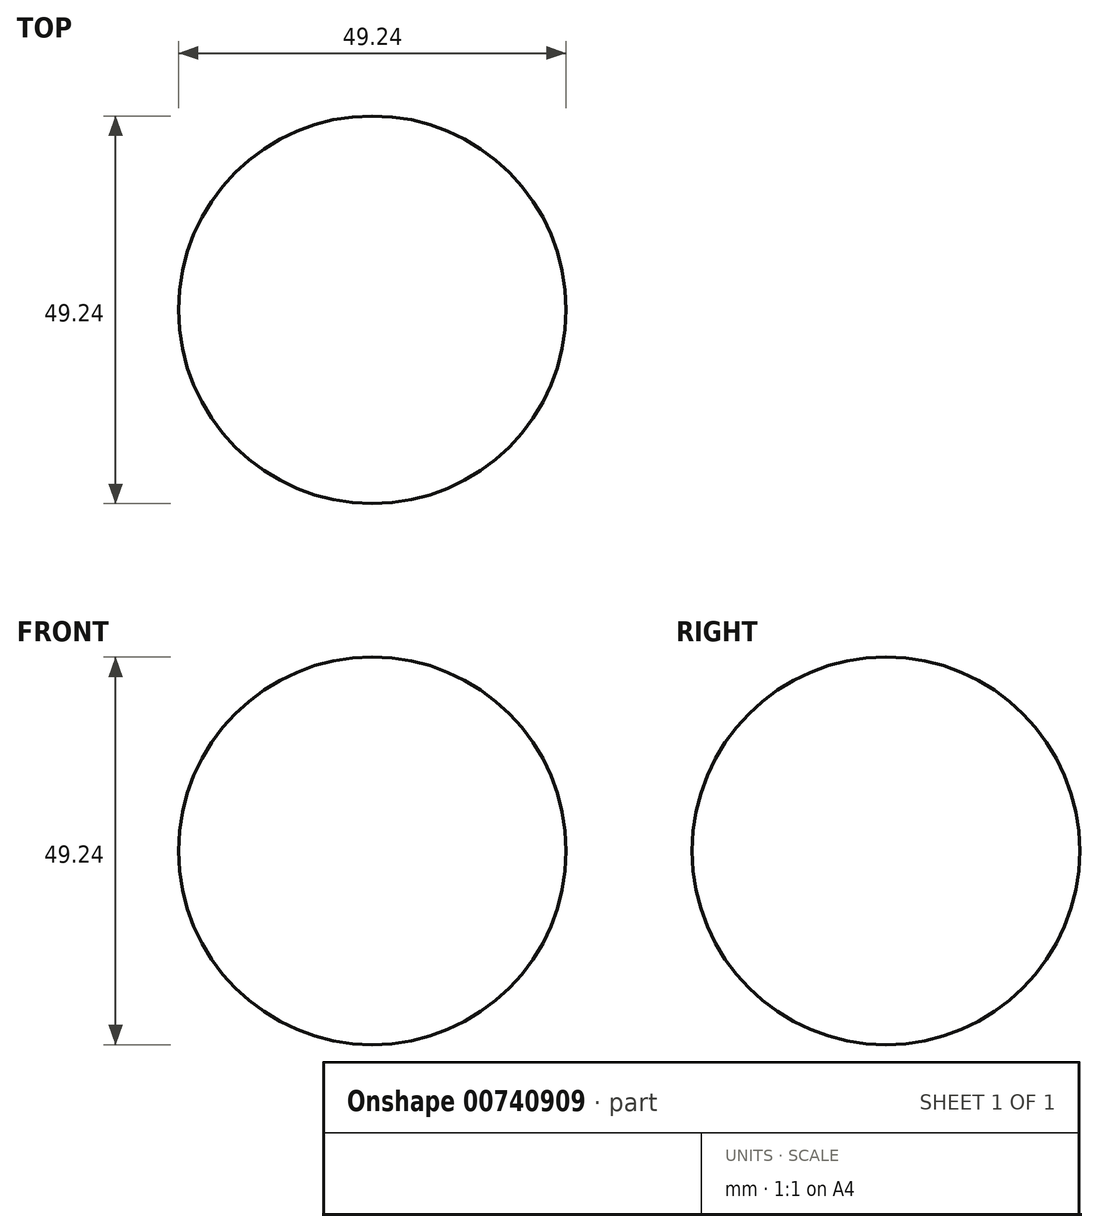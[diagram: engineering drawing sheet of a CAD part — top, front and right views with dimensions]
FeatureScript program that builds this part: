
annotation { "Feature Type Name" : "Feature", "Feature Type Description" : "" }
export const myFeature = defineFeature(function(context is Context, id is Id, definition is map)
    precondition{}
    {
        {
            var Q0;
            Q0=qCreatedBy(makeId("Top.planeOp"),FACE);
            var sketch = newSketch(context, id + "F0", { "sketchPlane" : qUnion([Q0])});
            skCircle(sketch, "E0", {"center": v(0, 0) * mm, "radius": 24.62 * mm});
            skLineSegment(sketch, "E1", {"start": v(0, 32.55) * mm, "end": v(0, -39.97) * mm});
            skSolve(sketch);
        }
        {
            var Q0;
            {var subQ0=sQuery(id+"F0.wireOp",EDGE,"E1");var subQ1=sQuery(id+"F0.wireOp",EDGE,"E0");var subQ2=makeQuery(id+"F0.imprint","INTERSECT",VERTEX,{"disambiguationData":[OD(0.0)],"derivedFrom":[subQ1,subQ0]});Q0=makeQuery(id+"F0.imprint","IMPRINT",FACE,{"disambiguationData":[TD([[makeQuery(id+"F0.imprint","IMPRINT",EDGE,{"disambiguationData":[TD([[subQ2,-1.0]])],"derivedFrom":subQ1}),1.0]])]});}
            var Q1;
            Q1=sQuery(id+"F0.wireOp",EDGE,"E1");
            revolve(context, id + "F1", {"surfaceOperationType" : NewSurfaceOperationType.NEW, "entities" : qUnion([Q0]), "axis" : qUnion([Q1]), "revolveType" : RevolveType.FULL});
        }
    });
